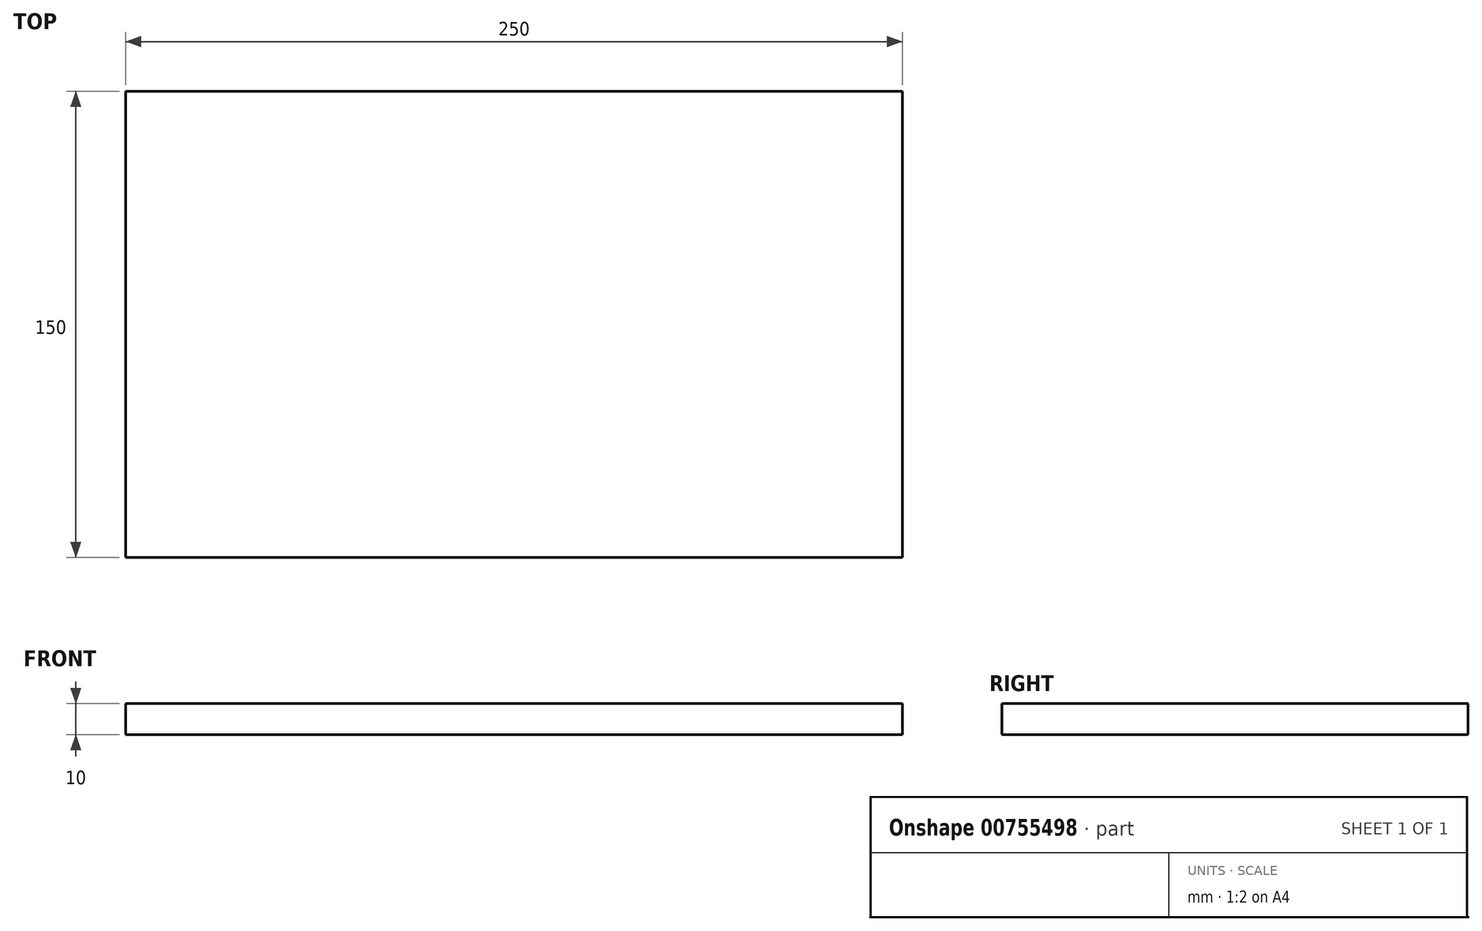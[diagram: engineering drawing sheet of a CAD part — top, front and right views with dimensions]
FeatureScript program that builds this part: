
annotation { "Feature Type Name" : "Feature", "Feature Type Description" : "" }
export const myFeature = defineFeature(function(context is Context, id is Id, definition is map)
    precondition{}
    {
        {
            var Q0;
            Q0=qCreatedBy(makeId("Top.planeOp"),FACE);
            var sketch = newSketch(context, id + "F0", { "sketchPlane" : qUnion([Q0])});
            skLineSegment(sketch, "E0.bottom", {"start": v(0, 150) * mm, "end": v(250, 150) * mm});
            skLineSegment(sketch, "E0.top", {"start": v(0, 0) * mm, "end": v(250, 0) * mm});
            skLineSegment(sketch, "E0.left", {"start": v(0, 150) * mm, "end": v(0, 0) * mm});
            skLineSegment(sketch, "E0.right", {"start": v(250, 150) * mm, "end": v(250, 0) * mm});
            skSolve(sketch);
        }
        {
            var Q0;
            Q0 = qSketchRegion(id + "F0", true);
            var Q1;
            Q1=makeQuery(id+"F0.imprint","IMPRINT",FACE,{"disambiguationData":[TD([[makeQuery(id+"F0.imprint","IMPRINT",EDGE,{"derivedFrom":sQuery(id+"F0.wireOp",EDGE,"Os8VYix5-OmMf-ISQN-eucH-URjKhtQXkReQ.bottom")}),-1.0]])]});
            extrude(context, id + "F1", {"entities" : qUnion([Q0, Q1]), "oppositeDirection" : true, "depth" : 10 * mm, "offsetDistance" : 25 * mm});
        }
    });
